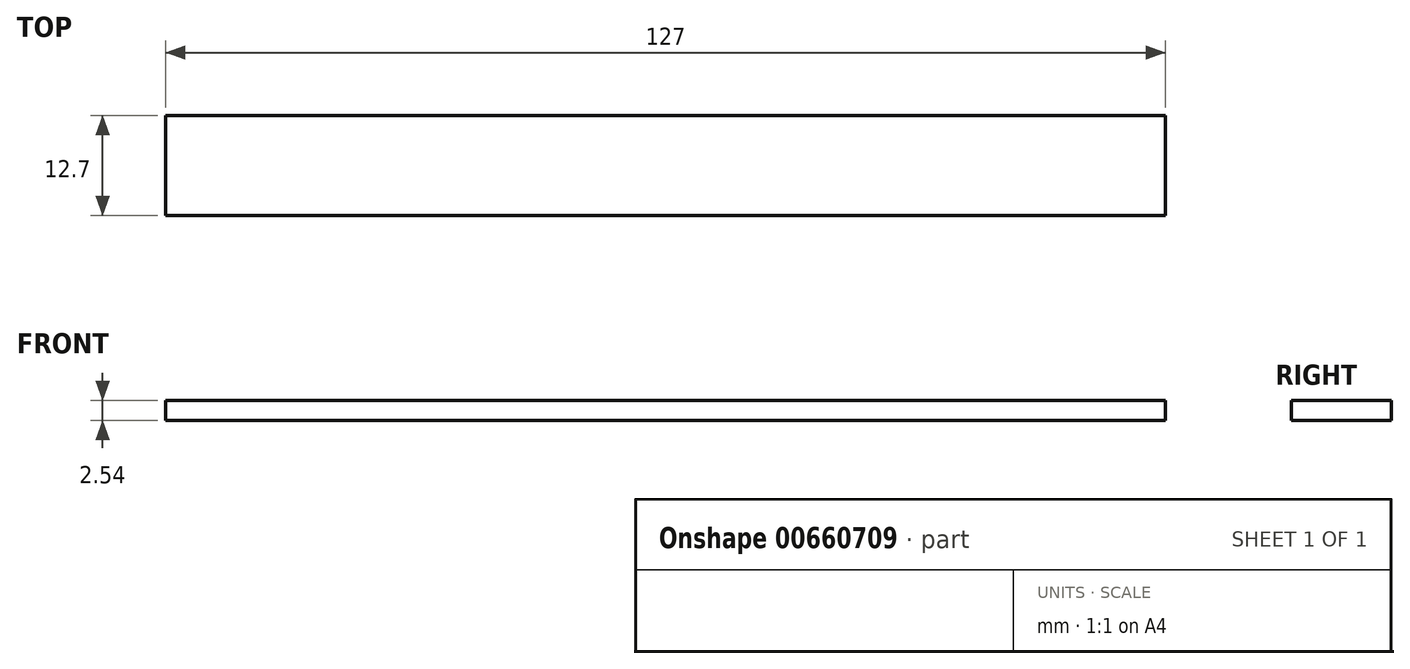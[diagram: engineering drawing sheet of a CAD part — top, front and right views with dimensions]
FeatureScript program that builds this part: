
annotation { "Feature Type Name" : "Feature", "Feature Type Description" : "" }
export const myFeature = defineFeature(function(context is Context, id is Id, definition is map)
    precondition{}
    {
        {
            var Q0;
            Q0=qCreatedBy(makeId("Top.planeOp"),FACE);
            var sketch = newSketch(context, id + "F0", { "sketchPlane" : qUnion([Q0])});
            skLineSegment(sketch, "E0.bottom", {"start": v(0, 12.7) * mm, "end": v(127, 12.7) * mm});
            skLineSegment(sketch, "E0.top", {"start": v(0, 0) * mm, "end": v(127, 0) * mm});
            skLineSegment(sketch, "E0.left", {"start": v(0, 12.7) * mm, "end": v(0, 0) * mm});
            skLineSegment(sketch, "E0.right", {"start": v(127, 12.7) * mm, "end": v(127, 0) * mm});
            skSolve(sketch);
        }
        {
            var Q0;
            {var subQ0=sQuery(id+"F0.wireOp",EDGE,"E0.left");Q0=makeQuery(id+"F0.imprint","IMPRINT",FACE,{"disambiguationData":[TD([[makeQuery(id+"F0.imprint","IMPRINT",EDGE,{"derivedFrom":subQ0}),1.0]])]});}
            var Q1;
            {var subQ0=sQuery(id+"F0.wireOp",EDGE,"E0.right");Q1=makeQuery(id+"F0.imprint","IMPRINT",FACE,{"disambiguationData":[TD([[makeQuery(id+"F0.imprint","IMPRINT",EDGE,{"derivedFrom":subQ0}),-1.0]])]});}
            var Q2;
            {var subQ0=sQuery(id+"F0.wireOp",EDGE,"RE1VgmHk-rfUn-HUX2-O9K4-JQGVitDNmmnu");var subQ1=sQuery(id+"F0.wireOp",EDGE,"E0.bottom");var subQ2=makeQuery(id+"F0.imprint","INTERSECT",VERTEX,{"disambiguationData":[OD(1.0)],"derivedFrom":[subQ1,subQ0]});Q2=makeQuery(id+"F0.imprint","IMPRINT",FACE,{"disambiguationData":[TD([[makeQuery(id+"F0.imprint","IMPRINT",EDGE,{"disambiguationData":[TD([[subQ2,-1.0]])],"derivedFrom":subQ1}),-1.0]])]});}
            var Q3;
            Q3=makeQuery(id+"FIPsjz87zek6mWJ_1.imprint","IMPRINT",FACE,{"disambiguationData":[TD([[makeQuery(id+"FIPsjz87zek6mWJ_1.imprint","IMPRINT",EDGE,{"derivedFrom":sQuery(id+"FIPsjz87zek6mWJ_1.wireOp",EDGE,"e65643e8-b480-4de8-9f89-3052c8ad30b5.bottom")}),-1.0]])]});
            extrude(context, id + "F1", {"entities" : qUnion([Q0, Q1, Q2, Q3]), "depth" : 2.54 * mm, "offsetDistance" : 25.4 * mm});
        }
    });
